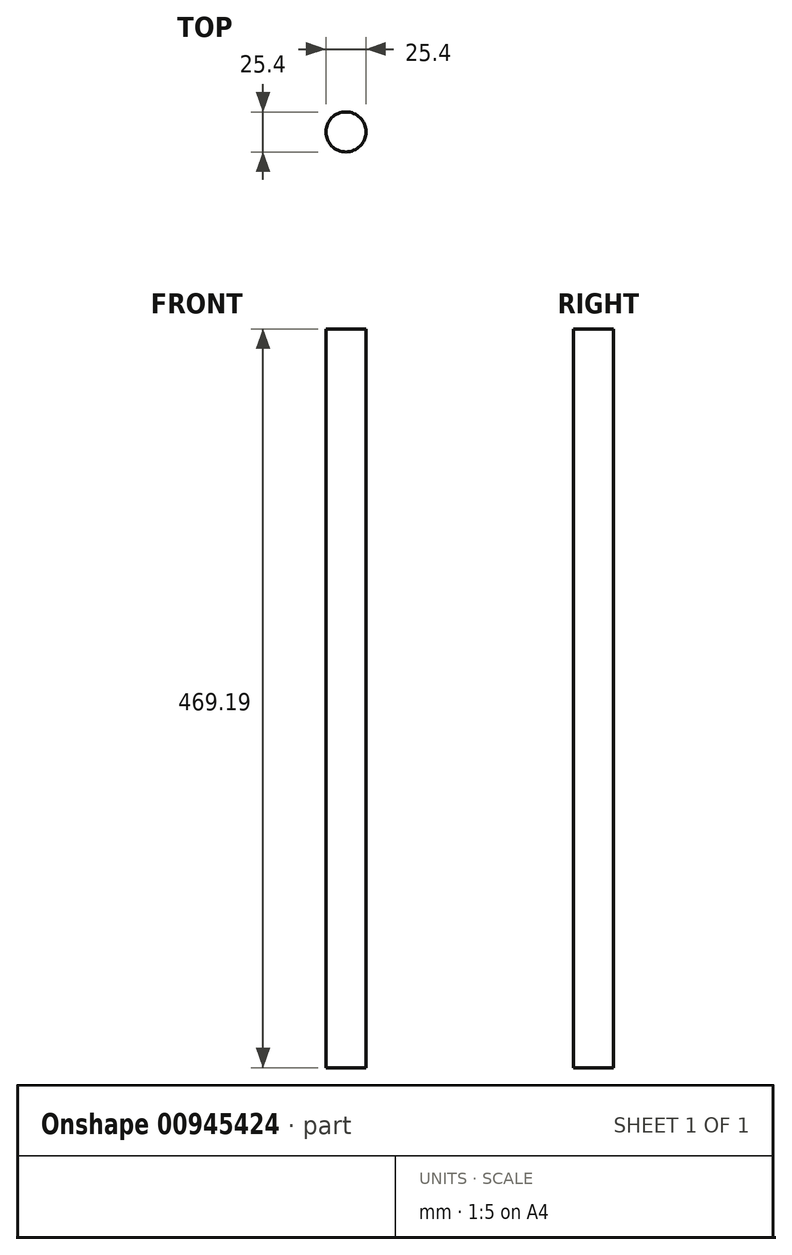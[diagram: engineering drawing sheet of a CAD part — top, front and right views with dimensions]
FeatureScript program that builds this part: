
annotation { "Feature Type Name" : "Feature", "Feature Type Description" : "" }
export const myFeature = defineFeature(function(context is Context, id is Id, definition is map)
    precondition{}
    {
        {
            var Q0;
            Q0=qCreatedBy(makeId("Top.planeOp"),FACE);
            var sketch = newSketch(context, id + "F0", { "sketchPlane" : qUnion([Q0])});
            skCircle(sketch, "E0", {"center": v(0, 0) * mm, "radius": 12.7 * mm});
            skSolve(sketch);
        }
        {
            var Q0;
            Q0=sQuery(id+"F0.wireOp",EDGE,"E0");
            extrude(context, id + "F1", {"bodyType" : ToolBodyType.SURFACE, "surfaceEntities" : qUnion([Q0]), "depth" : 469.2 * mm, "offsetDistance" : 25.4 * mm});
        }
    });
